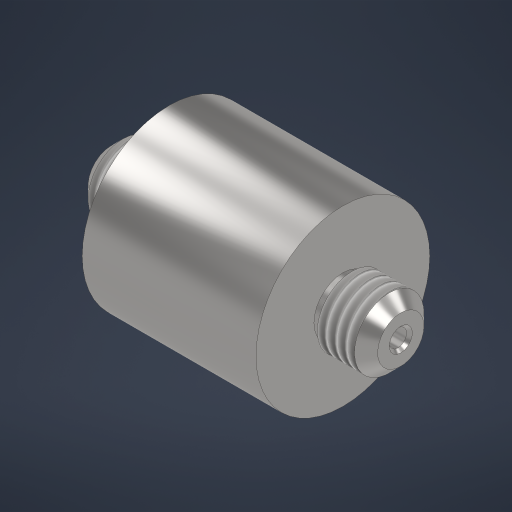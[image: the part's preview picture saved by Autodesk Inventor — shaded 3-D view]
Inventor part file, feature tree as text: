
AUTODESK INVENTOR PART (.ipt)
format: ipt  version: 2024.3 (Build 283343000, 343)  size: 291,328 bytes
history: native  units: mm
features: sketch x2, revolve x2, chamfer x2, thread x1, hole x1
ambient origin geometry x8: Origin, YZ Plane, XZ Plane, XY Plane, X Axis, Y Axis, Z Axis, Center Point
bodies: Solid1 (feature_tree)
feature tree (8):
  sketch  "Sketch1"  dims[d0=30.0mm d1=12.0mm]
  revolve  "Revolution1"  [1 undecoded]
  revolve  "Revolution2"  Angle=60.0deg
  thread  "Thread2"  [1 undecoded]
  chamfer  "Chamfer1"  Distance=30.0mm
  chamfer  "Chamfer2"  Distance=50.0mm
  hole  "Hole1"  [1 undecoded]
  sketch  "Sketch2"  dims[d3=8.42265mm d5=60.0deg d6=10.0mm d7=30.0mm d8=50.0mm d9=10.297443mm d10=10.0mm d11=4.0mm d12=18.0mm d13=23.0mm d14=360.0deg d15=90.0deg d18=50.0mm d19=0.0mm d20=2.0mm d21=2.0mm d22=45.0deg d23=3.0mm d24=0.5mm d25=2.0mm d26=45.0deg d27=10.0mm d29=1.0mm d30=10.106mm d31=16.0mm d32=13.0mm d33=2.0mm d34=90.0deg d35=20.0mm d36=20.594885mm]
note: 3 required parameter values undecoded (feature->parameter linkage not recoverable at this tier; creation-order binding heuristic only, values carry confidence <= 0.55)